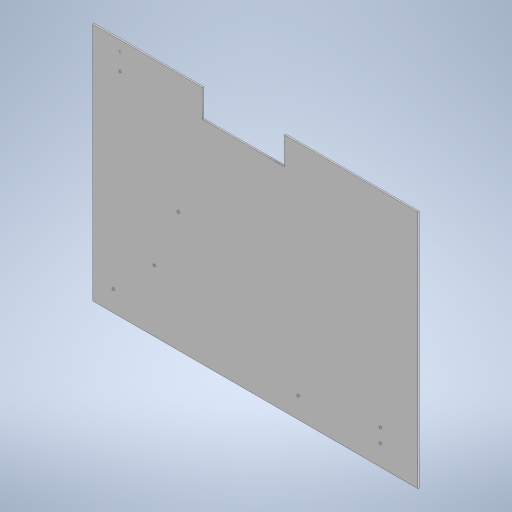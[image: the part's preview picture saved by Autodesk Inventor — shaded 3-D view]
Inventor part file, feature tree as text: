
AUTODESK INVENTOR PART (.ipt)
format: ipt  version: 2023 (Build 270158000, 158)  size: 218,112 bytes
history: native  units: mm
features: other x3, extrude x1, sketch x1, reference x1
ambient origin geometry x8: Origin, YZ Plane, XZ Plane, XY Plane, X Axis, Y Axis, Z Axis, Center Point
bodies: Solid1 (feature_tree)
feature tree (6):
  extrude  "Extrusion1"  [1 undecoded]
  sketch  "Sketch1"  dims[d0=2.0mm d1=0.0mm]
  reference  "Reference1"
  other  "<userpath>\ClawdDrive\Objet3D\IminaProbe\RoueMDF\Assembly1.iam"
  other  "Assembly1.iam"
  other  "Wheel2:1"
note: 1 required parameter value undecoded (feature->parameter linkage not recoverable at this tier; creation-order binding heuristic only, values carry confidence <= 0.55)
